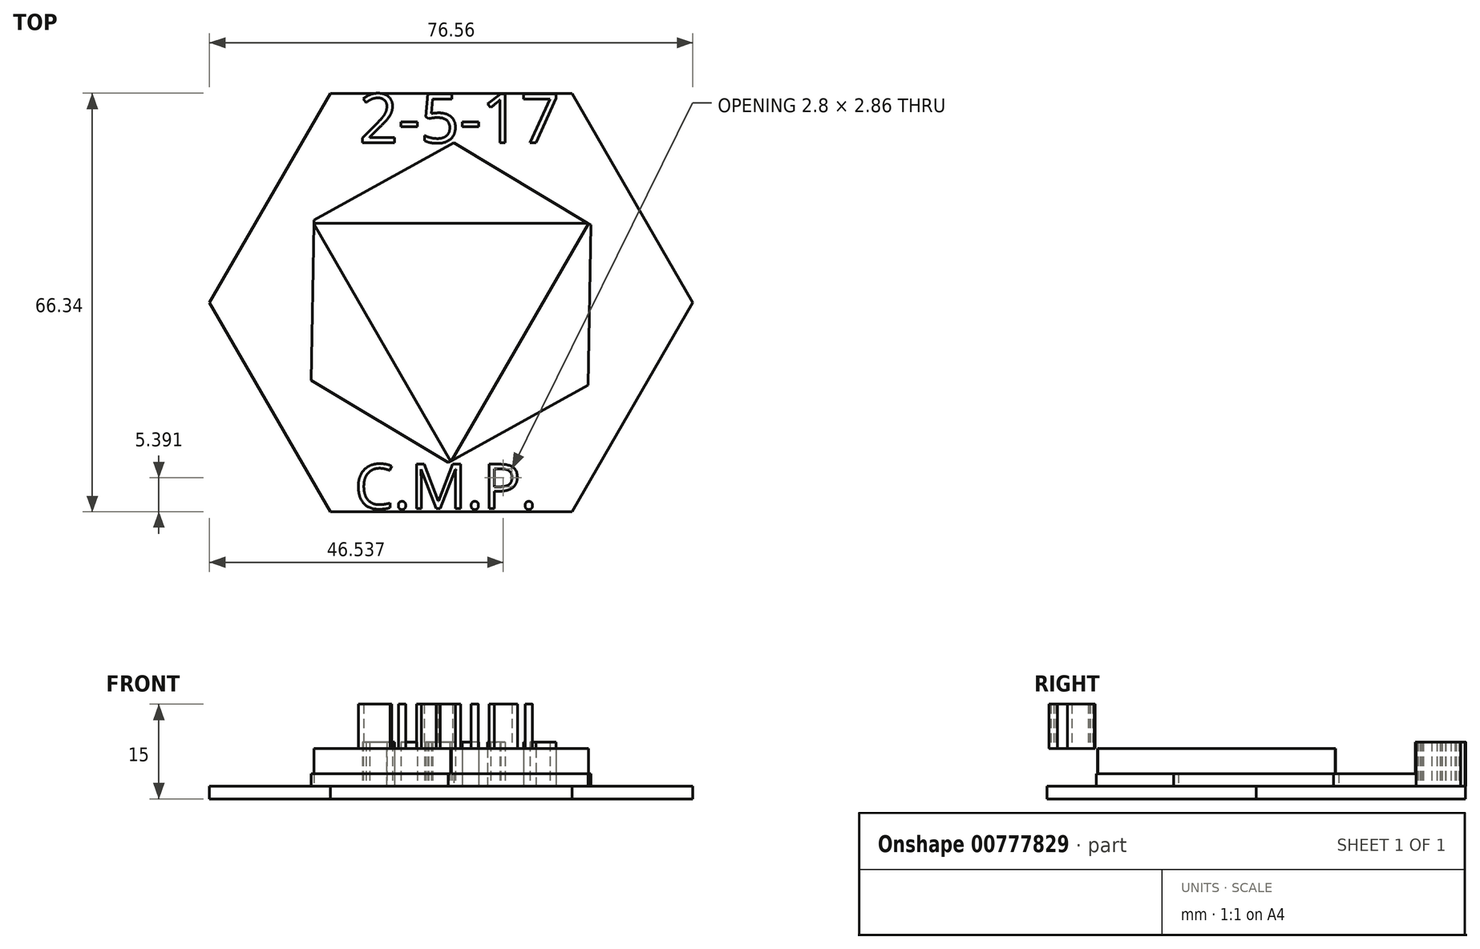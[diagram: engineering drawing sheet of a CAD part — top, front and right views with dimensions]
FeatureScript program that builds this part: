
annotation { "Feature Type Name" : "Feature", "Feature Type Description" : "" }
export const myFeature = defineFeature(function(context is Context, id is Id, definition is map)
    precondition{}
    {
        {
            var Q0;
            Q0=qCreatedBy(makeId("Top.planeOp"),FACE);
            var sketch = newSketch(context, id + "F0", { "sketchPlane" : qUnion([Q0])});
            skCircle(sketch, "E0.cCircle", {"center": v(0, 0) * mm, "radius": 33.15 * mm, "construction": true});
            skLineSegment(sketch, "E0.0", {"start": v(-19.14, 33.15) * mm, "end": v(19.14, 33.15) * mm});
            skLineSegment(sketch, "E0.1", {"start": v(19.14, 33.15) * mm, "end": v(38.28, 0) * mm});
            skLineSegment(sketch, "E0.2", {"start": v(38.28, 0) * mm, "end": v(19.14, -33.15) * mm});
            skLineSegment(sketch, "E0.3", {"start": v(19.14, -33.15) * mm, "end": v(-19.14, -33.15) * mm});
            skLineSegment(sketch, "E0.4", {"start": v(-19.14, -33.15) * mm, "end": v(-38.28, 0) * mm});
            skLineSegment(sketch, "E0.5", {"start": v(-38.28, 0) * mm, "end": v(-19.14, 33.15) * mm});
            skPoint(sketch, "E0.0.midPoint", {"position": v(0, 33.15) * mm});
            skSolve(sketch);
        }
        {
            var Q0;
            Q0=makeQuery(id+"F0.imprint","IMPRINT",FACE,{"disambiguationData":[TD([[makeQuery(id+"F0.imprint","IMPRINT",EDGE,{"derivedFrom":sQuery(id+"F0.wireOp",EDGE,"E0.0")}),-1.0]])]});
            extrude(context, id + "F1", {"entities" : qUnion([Q0]), "depth" : 2 * mm, "offsetDistance" : 25.4 * mm});
        }
        {
            var Q0;
            Q0=makeQuery(id+"F1.opExtrude","CAP_FACE",FACE,{"disambiguationData":[OSD([sQuery(id+"F0.wireOp",EDGE,"E0.0"),sQuery(id+"F0.wireOp",EDGE,"E0.1"),sQuery(id+"F0.wireOp",EDGE,"E0.2"),sQuery(id+"F0.wireOp",EDGE,"E0.3"),sQuery(id+"F0.wireOp",EDGE,"E0.4"),sQuery(id+"F0.wireOp",EDGE,"E0.5")])],"isStart":false});
            var sketch = newSketch(context, id + "F2", { "sketchPlane" : qUnion([Q0])});
            skCircle(sketch, "E1.cCircle", {"center": v(0, 0) * mm, "radius": 21.96 * mm, "construction": true});
            skLineSegment(sketch, "E1.0", {"start": v(-21.73, 13.06) * mm, "end": v(0.45, 25.35) * mm});
            skLineSegment(sketch, "E1.1", {"start": v(0.45, 25.35) * mm, "end": v(22.18, 12.3) * mm});
            skLineSegment(sketch, "E1.2", {"start": v(22.18, 12.3) * mm, "end": v(21.73, -13.06) * mm});
            skLineSegment(sketch, "E1.3", {"start": v(21.73, -13.06) * mm, "end": v(-0.45, -25.35) * mm});
            skLineSegment(sketch, "E1.4", {"start": v(-0.45, -25.35) * mm, "end": v(-22.18, -12.3) * mm});
            skLineSegment(sketch, "E1.5", {"start": v(-22.18, -12.3) * mm, "end": v(-21.73, 13.06) * mm});
            skPoint(sketch, "E1.0.midPoint", {"position": v(-10.64, 19.2) * mm});
            skSolve(sketch);
        }
        {
            var Q0;
            Q0=makeQuery(id+"F2.imprint","IMPRINT",FACE,{"disambiguationData":[TD([[makeQuery(id+"F2.imprint","IMPRINT",EDGE,{"derivedFrom":sQuery(id+"F2.wireOp",EDGE,"E1.0")}),-1.0]])]});
            extrude(context, id + "F3", {"entities" : qUnion([Q0]), "operationType" : NewBodyOperationType.ADD, "depth" : 2 * mm, "offsetDistance" : 25.4 * mm});
        }
        {
            var Q0;
            Q0=makeQuery(id+"F3.opExtrude","CAP_FACE",FACE,{"disambiguationData":[OSD([sQuery(id+"F2.wireOp",EDGE,"E1.0"),sQuery(id+"F2.wireOp",EDGE,"E1.1"),sQuery(id+"F2.wireOp",EDGE,"E1.2"),sQuery(id+"F2.wireOp",EDGE,"E1.3"),sQuery(id+"F2.wireOp",EDGE,"E1.4"),sQuery(id+"F2.wireOp",EDGE,"E1.5")])],"isStart":false});
            var sketch = newSketch(context, id + "F4", { "sketchPlane" : qUnion([Q0])});
            skCircle(sketch, "E2.cCircle", {"center": v(0, 0) * mm, "radius": 12.6 * mm, "construction": true});
            skLineSegment(sketch, "E2.0", {"start": v(-21.83, 12.6) * mm, "end": v(21.83, 12.6) * mm});
            skLineSegment(sketch, "E2.1", {"start": v(21.83, 12.6) * mm, "end": v(0, -25.2) * mm});
            skLineSegment(sketch, "E2.2", {"start": v(0, -25.2) * mm, "end": v(-21.83, 12.6) * mm});
            skPoint(sketch, "E2.0.midPoint", {"position": v(0, 12.6) * mm});
            skSolve(sketch);
        }
        {
            var Q0;
            {var subQ3=makeQuery(id+"F3.opExtrude","CAP_EDGE",EDGE,{"disambiguationData":[OSD([sQuery(id+"F2.wireOp",EDGE,"E1.5")])],"isStart":false});var subQ5=sQuery(id+"F4.wireOp",EDGE,"E2.0");var subQ11=makeQuery(id+"F4.imprint","INTERSECT",VERTEX,{"derivedFrom":[subQ3,subQ5]});Q0=makeQuery(id+"F4.imprint","IMPRINT",FACE,{"disambiguationData":[TD([[makeQuery(id+"F4.imprint","IMPRINT",EDGE,{"disambiguationData":[TD([[subQ11,-1.0]])],"derivedFrom":subQ5}),-1.0]])]});}
            extrude(context, id + "F5", {"entities" : qUnion([Q0]), "operationType" : NewBodyOperationType.ADD, "depth" : 4 * mm, "offsetDistance" : 25.4 * mm});
        }
        {
            var Q0;
            Q0=makeQuery(id+"F5.opExtrude","CAP_FACE",FACE,{"disambiguationData":[OSD([sQuery(id+"F2.wireOp",EDGE,"E1.1"),sQuery(id+"F2.wireOp",EDGE,"E1.3"),sQuery(id+"F2.wireOp",EDGE,"E1.5"),sQuery(id+"F4.wireOp",EDGE,"E2.0"),sQuery(id+"F4.wireOp",EDGE,"E2.1"),sQuery(id+"F4.wireOp",EDGE,"E2.2")])],"isStart":false});
            var sketch = newSketch(context, id + "F6", { "sketchPlane" : qUnion([Q0])});
            skLineSegment(sketch, "E3", {"start": v(-14.31, 9.42) * mm, "end": v(-6.24, 9.42) * mm});
            skLineSegment(sketch, "E4", {"start": v(-6.24, 9.42) * mm, "end": v(-10.64, 0) * mm});
            skLineSegment(sketch, "E5", {"start": v(5.02, 9.42) * mm, "end": v(5.02, 0) * mm});
            skLineSegment(sketch, "E6", {"start": v(12.11, 9.42) * mm, "end": v(12.11, 0) * mm});
            skSolve(sketch);
        }
        {
            var Q0;
            Q0=sQuery(id+"F6.wireOp",EDGE,"E3");
            var Q1;
            Q1=sQuery(id+"F6.wireOp",EDGE,"E4");
            var Q2;
            Q2=sQuery(id+"F6.wireOp",EDGE,"E5");
            var Q3;
            Q3=sQuery(id+"F6.wireOp",EDGE,"E6");
            extrude(context, id + "F7", {"bodyType" : ToolBodyType.SURFACE, "surfaceEntities" : qUnion([Q0, Q1, Q2, Q3]), "depth" : 3 * mm, "offsetDistance" : 25.4 * mm});
        }
        {
            var Q0;
            Q0=makeQuery(id+"F5.opExtrude","CAP_FACE",FACE,{"disambiguationData":[OSD([sQuery(id+"F2.wireOp",EDGE,"E1.1"),sQuery(id+"F2.wireOp",EDGE,"E1.3"),sQuery(id+"F2.wireOp",EDGE,"E1.5"),sQuery(id+"F4.wireOp",EDGE,"E2.0"),sQuery(id+"F4.wireOp",EDGE,"E2.1"),sQuery(id+"F4.wireOp",EDGE,"E2.2")])],"isStart":false});
            var sketch = newSketch(context, id + "F8", { "sketchPlane" : qUnion([Q0])});
            skText(sketch, "E7", { "text": "C.M.P.", "fontName": "OpenSans-Regular.ttf"});
            const initialGuessF8  = {"E7": [-0.0153, -0.03266, 1, 0, 0.0071]};
            skSetInitialGuess(sketch, initialGuessF8);
            skSolve(sketch);
        }
        {
            var Q0;
            Q0 = qSketchRegion(id + "F8", true);
            extrude(context, id + "F9", {"entities" : qUnion([Q0]), "depth" : 7 * mm, "offsetDistance" : 25.4 * mm});
        }
        {
            var Q0;
            Q0=makeQuery(id+"F1.opExtrude","CAP_FACE",FACE,{"disambiguationData":[OSD([sQuery(id+"F0.wireOp",EDGE,"E0.0"),sQuery(id+"F0.wireOp",EDGE,"E0.1"),sQuery(id+"F0.wireOp",EDGE,"E0.2"),sQuery(id+"F0.wireOp",EDGE,"E0.3"),sQuery(id+"F0.wireOp",EDGE,"E0.4"),sQuery(id+"F0.wireOp",EDGE,"E0.5")])],"isStart":false});
            var sketch = newSketch(context, id + "F10", { "sketchPlane" : qUnion([Q0])});
            skText(sketch, "E8", { "text": "2-5-17", "fontName": "OpenSans-Regular.ttf"});
            const initialGuessF10  = {"E8": [-0.01456, 0.02535, 1, 0, 0.0078]};
            skSetInitialGuess(sketch, initialGuessF10);
            skSolve(sketch);
        }
        {
            var Q0;
            Q0 = qSketchRegion(id + "F10", true);
            extrude(context, id + "F11", {"entities" : qUnion([Q0]), "operationType" : NewBodyOperationType.ADD, "depth" : 7 * mm, "offsetDistance" : 25.4 * mm});
        }
    });
